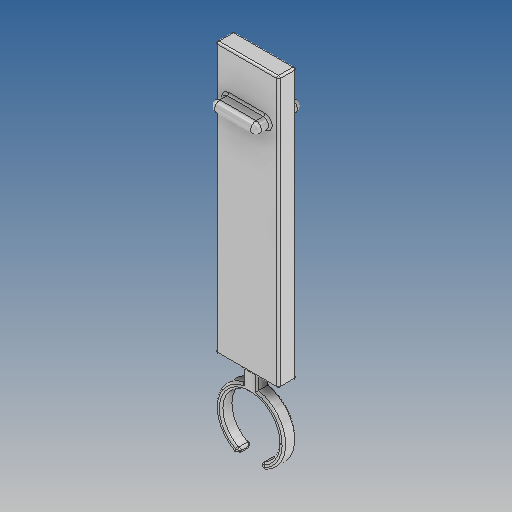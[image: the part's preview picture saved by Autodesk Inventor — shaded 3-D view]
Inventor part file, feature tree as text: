
AUTODESK INVENTOR PART (.ipt)
format: ipt  version: 2021 (Build 250183000, 183)  size: 395,776 bytes
history: native  units: mm
features: fillet x8, extrude x4, sketch x4, plane x1
ambient origin geometry x8: Origin, YZ Plane, XZ Plane, XY Plane, X Axis, Y Axis, Z Axis, Center Point
bodies: Solid1 (feature_tree)
feature tree (17):
  extrude  "Extrusion1"  Depth=150.0mm
  extrude  "Extrusion2"  Depth=3.0mm
  plane  "Work Plane1"
  extrude  "Extrusion4"  Depth=25.0mm
  fillet  "Fillet1"  Radius=17.5mm
  fillet  "Fillet2"  Radius=8.0mm
  fillet  "Fillet3"  [1 undecoded]
  fillet  "Fillet4"  Radius=41.0mm
  fillet  "Fillet5"  Radius=8.0mm
  fillet  "Fillet6"  Radius=13.5mm
  fillet  "Fillet7"  Radius=38.0mm
  fillet  "Fillet8"  Radius=31.75mm
  sketch  "Sketch1"  dims[d0=35.0mm d1=150.0mm]
  sketch  "Sketch2"  dims[d2=10.0mm d3=0.0mm d4=3.0mm]
  sketch  "Sketch4"  dims[d11=20.0mm d12=25.0mm d19=17.5mm d20=8.0mm d21=0.0mm d29=-5.0mm d35=41.0mm d43=8.0mm d45=13.5mm d47=38.0mm d49=31.75mm]
  extrude  "Extrusion5"  Depth=6.0mm
  sketch  "Sketch5"  dims[d50=27.0mm d51=6.0mm d52=6.0mm d53=8.0mm d54=3.330286mm d55=3.330286mm d56=4.0mm d57=0.425824mm d58=13.5mm d59=90.0deg d60=7.0mm d61=0.0mm d62=2.0mm d63=1.0mm d64=1.0mm d65=3.0mm d66=1.0mm d67=1.0mm d68=17.5mm d69=25.0mm d70=3.0mm d71=20.0mm d73=0.0mm d74=8.0mm d75=3.0mm d76=1.0mm d77=0.5mm d78=0.872665mm d79=0.5mm d80=0.872665mm]
note: 1 required parameter value undecoded (feature->parameter linkage not recoverable at this tier; creation-order binding heuristic only, values carry confidence <= 0.55)
